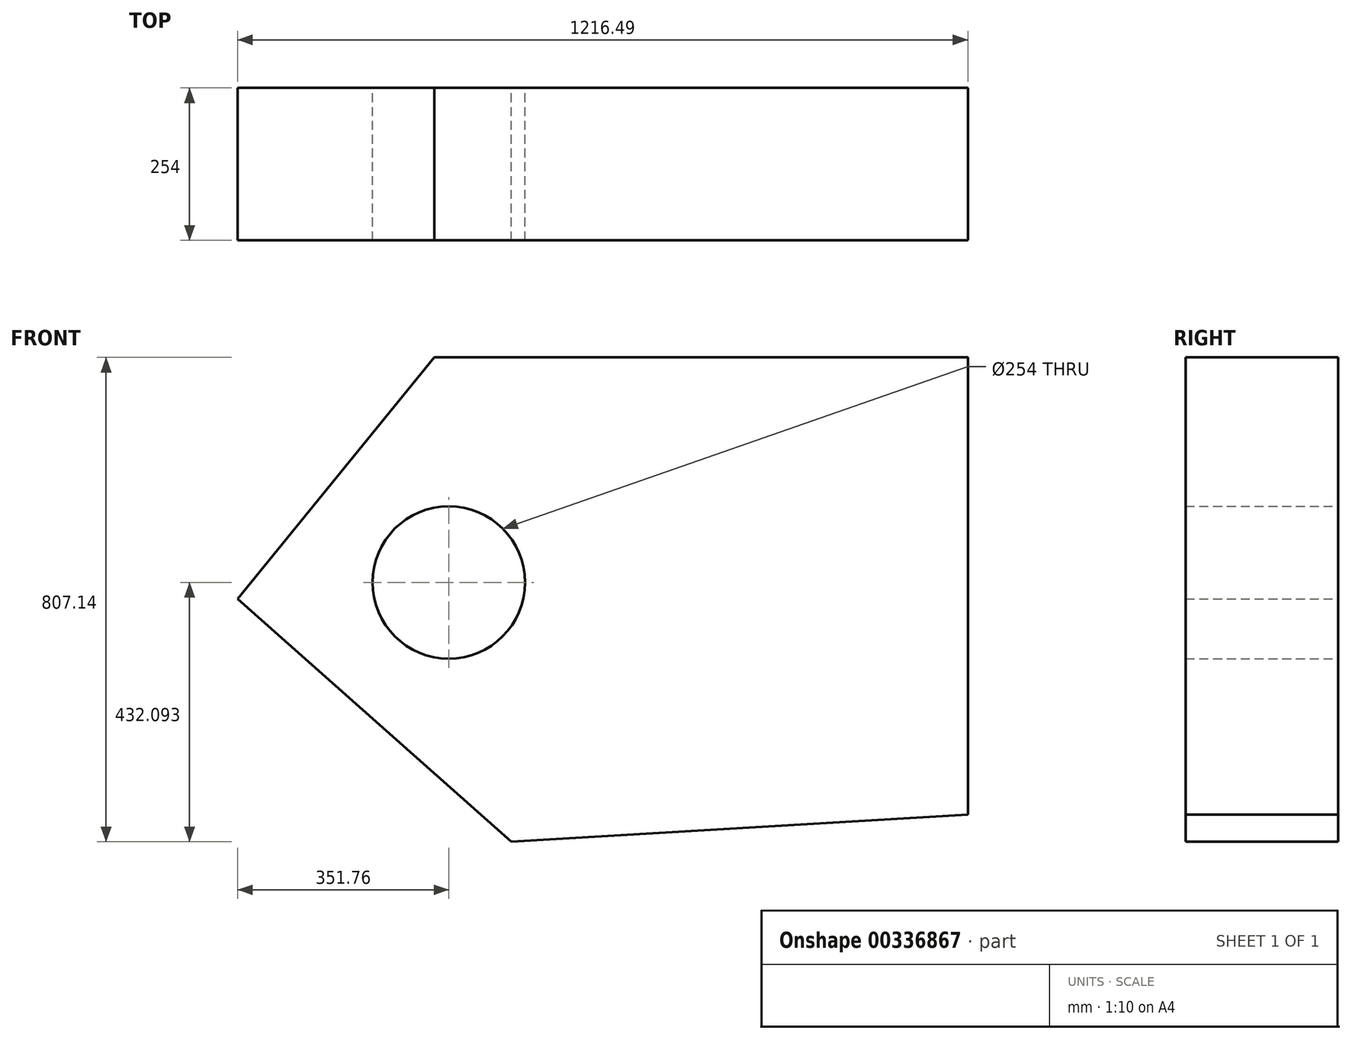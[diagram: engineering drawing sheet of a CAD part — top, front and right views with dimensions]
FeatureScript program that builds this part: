
annotation { "Feature Type Name" : "Feature", "Feature Type Description" : "" }
export const myFeature = defineFeature(function(context is Context, id is Id, definition is map)
    precondition{}
    {
        {
            var Q0;
            Q0=qCreatedBy(makeId("Front.planeOp"),FACE);
            var sketch = newSketch(context, id + "F0", { "sketchPlane" : qUnion([Q0])});
            skLineSegment(sketch, "E0", {"start": v(-327.5, 0) * mm, "end": v(0, 402.38) * mm});
            skLineSegment(sketch, "E1", {"start": v(0, 402.38) * mm, "end": v(889, 402.38) * mm});
            skLineSegment(sketch, "E2", {"start": v(889, 402.38) * mm, "end": v(889, -359.62) * mm});
            skLineSegment(sketch, "E3", {"start": v(889, -359.62) * mm, "end": v(128.34, -404.76) * mm});
            skLineSegment(sketch, "E4", {"start": v(128.34, -404.76) * mm, "end": v(-327.5, 0) * mm});
            skCircle(sketch, "E5", {"center": v(24.27, 27.33) * mm, "radius": 127 * mm});
            skSolve(sketch);
        }
        {
            var Q0;
            Q0=makeQuery(id+"F0.imprint","IMPRINT",FACE,{"disambiguationData":[TD([[makeQuery(id+"F0.imprint","IMPRINT",EDGE,{"derivedFrom":sQuery(id+"F0.wireOp",EDGE,"E0")}),-1.0]])]});
            extrude(context, id + "F1", {"entities" : qUnion([Q0]), "depth" : 254 * mm});
        }
    });
